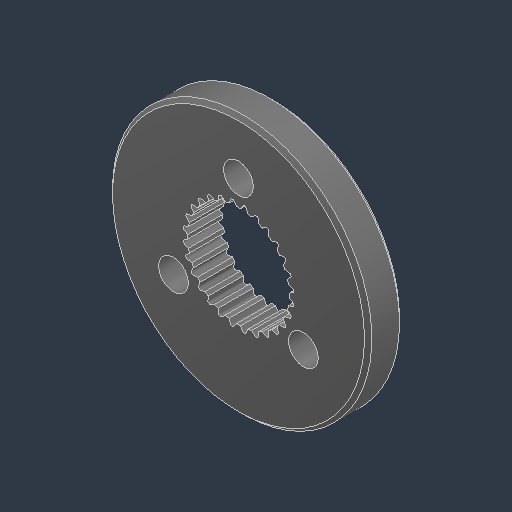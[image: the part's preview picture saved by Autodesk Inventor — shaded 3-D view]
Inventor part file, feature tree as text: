
AUTODESK INVENTOR PART (.ipt)
format: ipt  version: 2024.3 (Build 283343000, 343)  size: 243,712 bytes
history: native  units: in
note: dims shown in document units (in); Inventor stores cm internally (conversion verified against a paired STEP export)
features: chamfer x1
ambient origin geometry x8: Origin, YZ Plane, XZ Plane, XY Plane, X Axis, Y Axis, Z Axis, Center Point
bodies: Solid1 (feature_tree)
feature tree (1):
  chamfer  "Chamfer1"  [1 undecoded]
note: 1 required parameter value undecoded (feature->parameter linkage not recoverable at this tier; creation-order binding heuristic only, values carry confidence <= 0.55)
